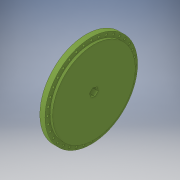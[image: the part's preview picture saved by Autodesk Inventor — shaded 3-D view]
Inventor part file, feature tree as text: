
AUTODESK INVENTOR PART (.ipt)
format: ipt  version: 2018 (Build 220112000, 112)  size: 167,936 bytes
history: native  units: in
note: dims shown in document units (in); Inventor stores cm internally (conversion verified against a paired STEP export)
features: extrude x3, sketch x3, pattern_circular x1, projected_geometry x1
ambient origin geometry x8: Origin, YZ Plane, XZ Plane, XY Plane, X Axis, Y Axis, Z Axis, Center Point
bodies: Solid1 (feature_tree)
feature tree (8):
  extrude  "Extrusion1"  Depth=0.38in
  extrude  "Extrusion2"  Depth=0.25in
  extrude  "Extrusion3"  Depth=0.25in
  pattern_circular  "Circular Pattern1"  [2 undecoded]
  sketch  "Sketch1"  dims[d0=4.5in d1=0.38in]
  sketch  "Sketch2"  dims[d2=0.25in d3=0.0in d4=4.015in]
  sketch  "Sketch3"  dims[d5=0.125in d6=0.0in d7=0.11in d8=2.125in d9=0.25in d10=0.0in d11=14.1732in d12=360.0deg]
  projected_geometry  "Projected Loop1"
note: 2 required parameter values undecoded (feature->parameter linkage not recoverable at this tier; creation-order binding heuristic only, values carry confidence <= 0.55)
